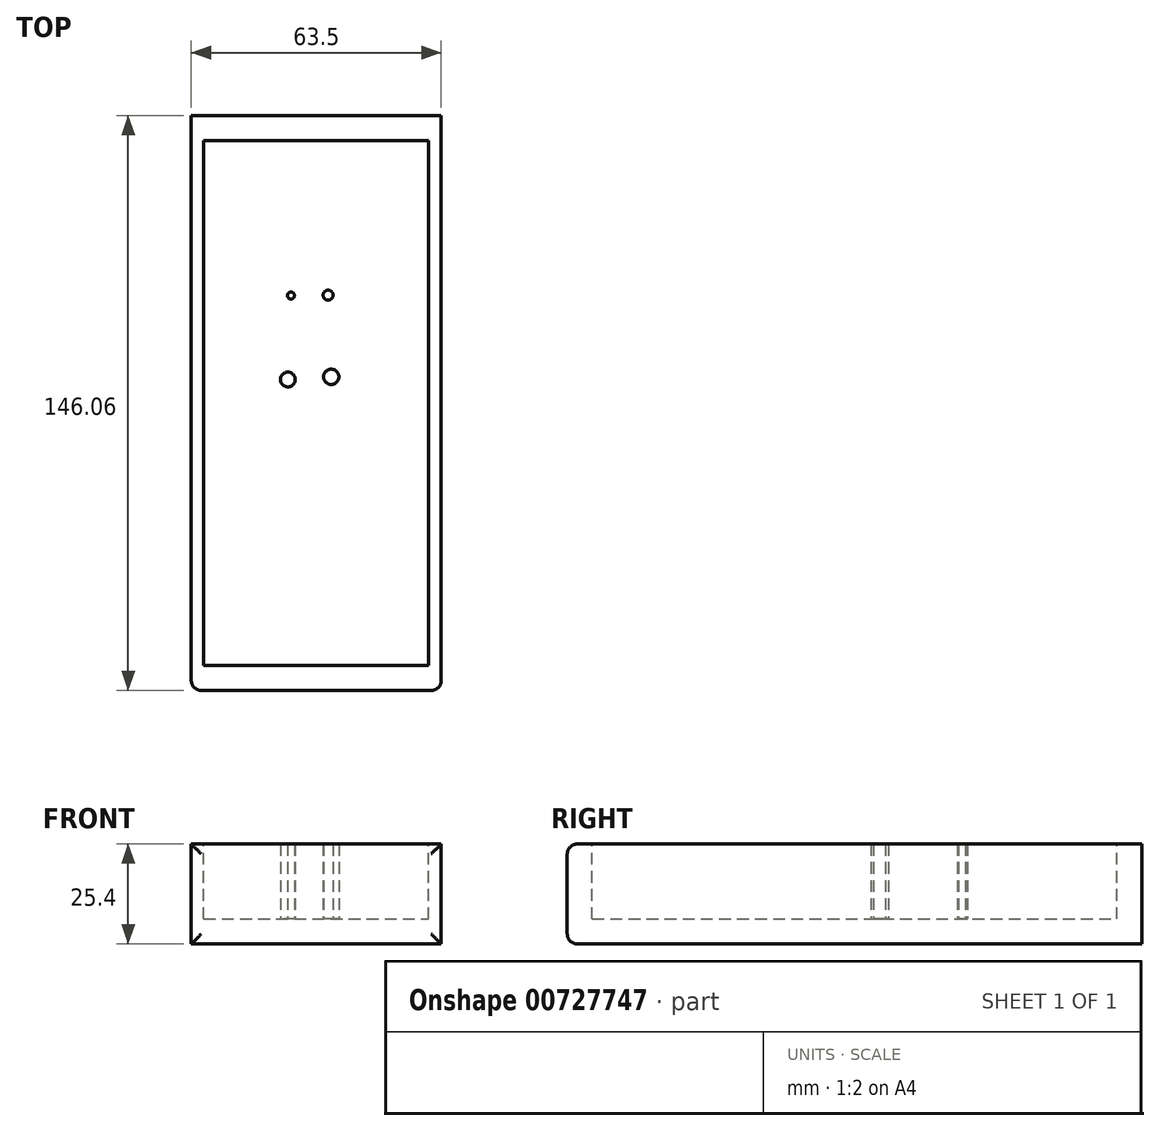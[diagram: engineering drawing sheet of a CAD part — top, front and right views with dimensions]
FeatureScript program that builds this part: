
annotation { "Feature Type Name" : "Feature", "Feature Type Description" : "" }
export const myFeature = defineFeature(function(context is Context, id is Id, definition is map)
    precondition{}
    {
        {
            var Q0;
            Q0=qCreatedBy(makeId("Top.planeOp"),FACE);
            var sketch = newSketch(context, id + "F0", { "sketchPlane" : qUnion([Q0])});
            skLineSegment(sketch, "E0.bottom", {"start": v(31.75, -73.03) * mm, "end": v(-31.75, -73.03) * mm});
            skLineSegment(sketch, "E0.top", {"start": v(31.75, 73.03) * mm, "end": v(-31.75, 73.03) * mm});
            skLineSegment(sketch, "E0.left", {"start": v(31.75, -73.03) * mm, "end": v(31.75, 73.03) * mm});
            skLineSegment(sketch, "E0.right", {"start": v(-31.75, -73.03) * mm, "end": v(-31.75, 73.03) * mm});
            skPoint(sketch, "E0.middle", {"position": v(0, 0) * mm});
            skSolve(sketch);
        }
        {
            var Q0;
            Q0 = qSketchRegion(id + "F0", true);
            extrude(context, id + "F1", {"entities" : qUnion([Q0]), "depth" : 25.4 * mm, "offsetDistance" : 25.4 * mm});
        }
        {
            var Q0;
            Q0=makeQuery(id+"F1.opExtrude","CAP_FACE",FACE,{"disambiguationData":[OSD([sQuery(id+"F0.wireOp",EDGE,"E0.bottom"),sQuery(id+"F0.wireOp",EDGE,"E0.top"),sQuery(id+"F0.wireOp",EDGE,"E0.left"),sQuery(id+"F0.wireOp",EDGE,"E0.right")])],"isStart":false});
            var sketch = newSketch(context, id + "F2", { "sketchPlane" : qUnion([Q0])});
            skLineSegment(sketch, "E1.bottom", {"start": v(-28.57, -66.68) * mm, "end": v(28.58, -66.68) * mm});
            skLineSegment(sketch, "E1.top", {"start": v(-28.58, 66.68) * mm, "end": v(28.57, 66.68) * mm});
            skLineSegment(sketch, "E1.left", {"start": v(-28.57, -66.68) * mm, "end": v(-28.58, 66.68) * mm});
            skLineSegment(sketch, "E1.right", {"start": v(28.58, -66.68) * mm, "end": v(28.57, 66.68) * mm});
            skPoint(sketch, "E1.middle", {"position": v(0, 0) * mm});
            skSolve(sketch);
        }
        {
            var Q0;
            Q0 = qSketchRegion(id + "F2", true);
            extrude(context, id + "F3", {"entities" : qUnion([Q0]), "operationType" : NewBodyOperationType.REMOVE, "oppositeDirection" : true, "depth" : 19.05 * mm, "offsetDistance" : 25.4 * mm});
        }
        {
            var Q0;
            Q0=makeQuery(id+"F3.boolean.opBoolean","COPY",FACE,{"derivedFrom":makeQuery(id+"F3.opExtrude","CAP_FACE",FACE,{"disambiguationData":[OSD([sQuery(id+"F2.wireOp",EDGE,"E1.bottom"),sQuery(id+"F2.wireOp",EDGE,"E1.top"),sQuery(id+"F2.wireOp",EDGE,"E1.left"),sQuery(id+"F2.wireOp",EDGE,"E1.right")])],"isStart":false})});
            var sketch = newSketch(context, id + "F4", { "sketchPlane" : qUnion([Q0])});
            skCircle(sketch, "E2", {"center": v(-6.44, 27.3) * mm, "radius": 0.9 * mm});
            skCircle(sketch, "E3", {"center": v(3, 27.4) * mm, "radius": 1.27 * mm});
            skCircle(sketch, "E4", {"center": v(-7.22, 5.97) * mm, "radius": 1.88 * mm});
            skCircle(sketch, "E5", {"center": v(3.79, 6.65) * mm, "radius": 1.95 * mm});
            skSolve(sketch);
        }
        {
            var Q0;
            Q0 = qSketchRegion(id + "F4", true);
            extrude(context, id + "F5", {"entities" : qUnion([Q0]), "operationType" : NewBodyOperationType.ADD, "depth" : 19.05 * mm, "offsetDistance" : 25.4 * mm});
        }
        {
            var Q0;
            Q0=makeQuery(id+"F1.opExtrude","SWEPT_FACE",FACE,{"disambiguationData":[OSD([sQuery(id+"F0.wireOp",EDGE,"E0.bottom")])]});
            fillet(context, id + "F6", {"entities" : qUnion([Q0]), "radius" : 2.54 * mm, "tangentPropagation" : true, "allowEdgeOverflow" : false});
        }
    });
